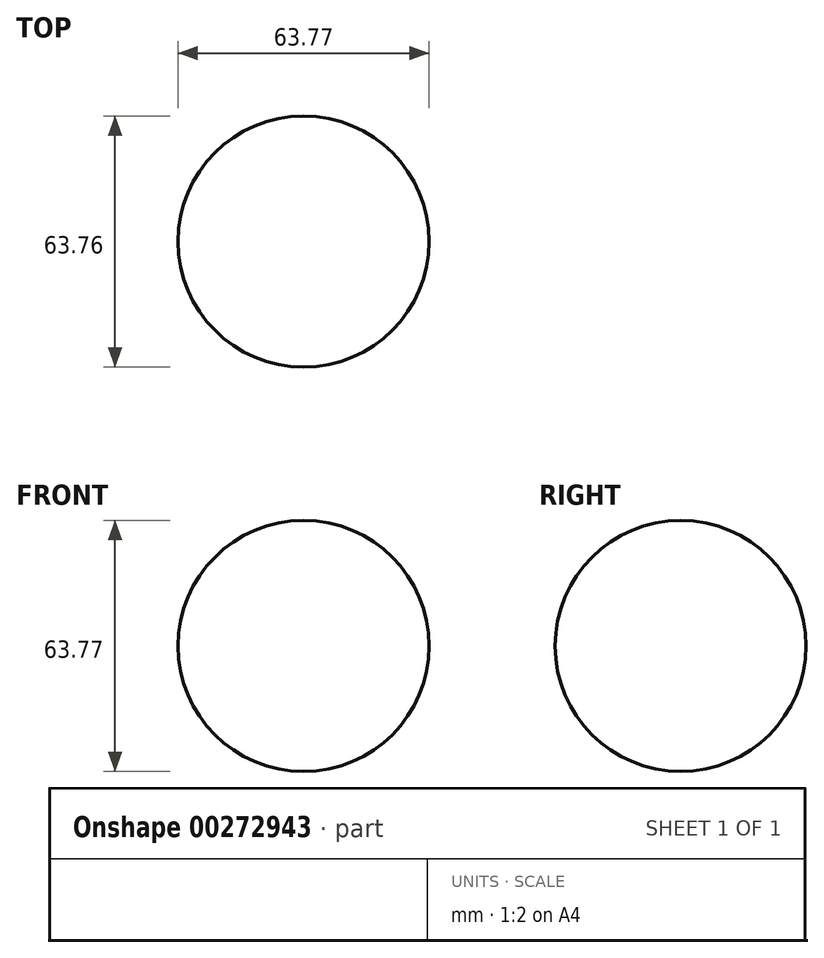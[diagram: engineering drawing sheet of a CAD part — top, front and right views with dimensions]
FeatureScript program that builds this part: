
annotation { "Feature Type Name" : "Feature", "Feature Type Description" : "" }
export const myFeature = defineFeature(function(context is Context, id is Id, definition is map)
    precondition{}
    {
        {
            var Q0;
            Q0=qCreatedBy(makeId("Front.planeOp"),FACE);
            var sketch = newSketch(context, id + "F0", { "sketchPlane" : qUnion([Q0])});
            skArc(sketch, "E0", {"start": v(-39.72, 62.25) * mm, "mid": v(-71.6, 30.36) * mm, "end": v(-39.72, -1.52) * mm});
            skLineSegment(sketch, "E1", {"start": v(-39.72, 62.25) * mm, "end": v(-39.72, -1.52) * mm});
            skSolve(sketch);
        }
        {
            var Q0;
            Q0=makeQuery(id+"F0.imprint","IMPRINT",FACE,{"disambiguationData":[TD([[makeQuery(id+"F0.imprint","IMPRINT",EDGE,{"derivedFrom":sQuery(id+"F0.wireOp",EDGE,"E0")}),1.0]])]});
            var Q1;
            Q1=sQuery(id+"F0.wireOp",EDGE,"E1");
            revolve(context, id + "F1", {"entities" : qUnion([Q0]), "axis" : qUnion([Q1]), "revolveType" : RevolveType.FULL});
        }
    });
